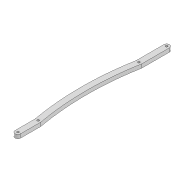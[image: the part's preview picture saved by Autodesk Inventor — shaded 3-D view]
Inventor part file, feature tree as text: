
AUTODESK INVENTOR PART (.ipt)
format: ipt  version: 2022 (Build 260153000, 153)  size: 105,984 bytes
history: native  units: mm
features: extrude x1, sketch x1
ambient origin geometry x8: Origin, YZ Plane, XZ Plane, XY Plane, X Axis, Y Axis, Z Axis, Center Point
bodies: Solid1 (feature_tree)
feature tree (2):
  extrude  "Extrusion1"  Depth=300.0mm
  sketch  "Sketch1"  dims[d0=2.2mm d1=2.2mm d2=6.0mm d3=158.319mm d6=4.0mm d7=0.0mm d10=2.2mm d11=21.572mm d12=2.2mm d13=128.76mm d16=300.0mm d17=300.0mm]
